# Revit family: Soft Square
name_source: partatom
category: Furniture
revit_build: Autodesk Revit 2016 (Build: 20151209_0715(x64)
units: mm (PartAtom-declared; Revit-internal decimal feet)

## family parameters
Always vertical = Yes
Cut with Voids When Loaded = No
OmniClass Number = 23.40.20.00
OmniClass Title = General Furniture and Specialties
Room Calculation Point = No
Shared = No
Work Plane-Based = No

## types (2) — shared parameters
Assembly Code = E2020200
Legs = Walnut
Manufacturer = Gresham Office Furniture
Range = GALLEN
Table Top = Gresham - White MFC
URL = www.gof.co.uk

## per-type parameters (varying)
| type | Depth | Product Code | Width |
| 800 x 800 x 435 | 800 mm  [stored 2.62467 ft] | GAL088 | 800 mm  [stored 2.62467 ft] |
| 600 x 600 x 435 | 600 mm | GAL066 | 600 mm |

note: [stored X ft] marks values corroborated as IEEE doubles in the binary element streams (Revit-internal decimal feet)

## geometry (parser evidence)
native form markers: Sweep x3
no freeform markers — native parametric forms only
